# Revit family: СЭТ_СИПУ
name_source: partatom
category: Электрические приборы
units: mm (PartAtom-declared; Revit-internal decimal feet)

## family parameters
Всегда вертикально = Да
Заголовок OmniClass = Information and Communication
Номер OmniClass = 23.85.00.00
Общий = Нет
Основа = Стена
При загрузке вырезать с полостями = Нет
Размер круглого соединителя = Использовать диаметр
Сохранять ориентацию аннотаций = Нет
Тип детали = Нормальный
Точка расчета площади = Нет

## types (14) — shared parameters
ADSK_Единица измерения = шт.
ADSK_Завод-изготовитель = Chronos Meter
ADSK_Количество = 1
ADSK_Наименование = Счетчик импульсов проводной универсальный (СИПУ)
Высота = 95 мм
Высота размещения (по ниж.грани) = 1500 мм
Глубина = 58 мм
Крепление = DIN
Сайт производителя = https://chronosmeter.com
Степень защиты = IP20

## per-type parameters (varying)
| type | ADSK_Код изделия | ADSK_Масса | Вход NAMUR | Интерфейс | Каналы | Минус полуширина | Полуширина | Ширина |
| SET.SIPU.RS.2.0.DIN | C208-06 | 0.15 | Нет | RS-485 | 2 | 19 мм | -19 мм | 37 мм |
| SET.SIPU.RS.2.N.DIN | C208-07 | 0.15 | Да | RS-485 | 2 | 19 мм | -19 мм | 37 мм |
| SET.SIPU.RS.4.0.DIN | C208-08 | 0.15 | Нет | RS-485 | 4 | 19 мм | -19 мм | 37 мм |
| SET.SIPU.RS.4.N.DIN | C208-09 | 0.15 | Да | RS-485 | 4 | 19 мм | -19 мм | 37 мм |
| SET.SIPU.RS.10.0.DIN | C208-10 | 0.3 | Нет | RS-485 | 10 | 36 мм | -36 мм | 71 мм |
| SET.SIPU.RS.10.N.DIN | C208-11 | 0.3 | Да | RS-485 | 10 | 36 мм | -36 мм | 71 мм |
| SET.SIPU.RS.16.0.DIN | C208-12 | 0.3 | Нет | RS-485 | 16 | 54 мм | -54 мм | 107 мм |
| SET.SIPU.MB.2.0.DIN | C208-19 | 0.15 | Нет | M-BUS | 2 | 19 мм | -19 мм | 37 мм |
| SET.SIPU.MB.2.N.DIN | C208-20 | 0.15 | Да | M-BUS | 2 | 19 мм | -19 мм | 37 мм |
| SET.SIPU.MB.4.0.DIN | C208-21 | 0.15 | Нет | M-BUS | 4 | 19 мм | -19 мм | 37 мм |
| SET.SIPU.MB.4.N.DIN | C208-22 | 0.15 | Да | M-BUS | 4 | 19 мм | -19 мм | 37 мм |
| SET.SIPU.MB.10.0.DIN | C208-23 | 0.3 | Нет | M-BUS | 10 | 36 мм | -36 мм | 71 мм |
| SET.SIPU.MB.10.N.DIN | C208-24 | 0.3 | Да | M-BUS | 10 | 36 мм | -36 мм | 71 мм |
| SET.SIPU.MB.16.0.DIN | C208-25 | 0.3 | Нет | M-BUS | 16 | 54 мм | -54 мм | 107 мм |

note: column(s) folded — value = type name in every type: ADSK_Марка
